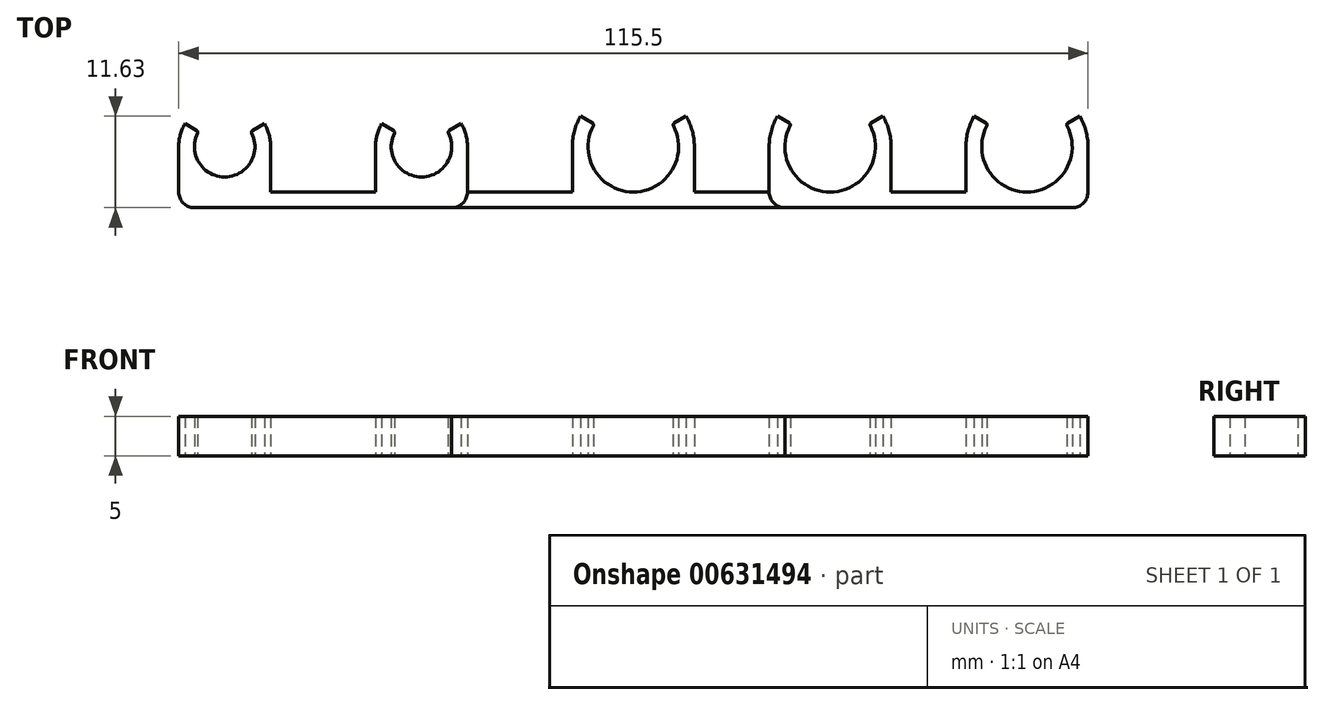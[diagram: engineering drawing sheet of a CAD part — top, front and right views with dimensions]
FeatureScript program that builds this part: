
annotation { "Feature Type Name" : "Feature", "Feature Type Description" : "" }
export const myFeature = defineFeature(function(context is Context, id is Id, definition is map)
    precondition{}
    {
        {
            var Q0;
            Q0=qCreatedBy(makeId("Top.planeOp"),FACE);
            var sketch = newSketch(context, id + "F0", { "sketchPlane" : qUnion([Q0])});
            skArc(sketch, "E0", {"start": v(-5.1, 2.67) * mm, "mid": v(0, -5.75) * mm, "end": v(5.1, 2.67) * mm});
            skArc(sketch, "E1.0", {"start": v(-6.7, 3.88) * mm, "mid": v(0, -7.75) * mm, "end": v(6.7, 3.88) * mm});
            skLineSegment(sketch, "E2", {"start": v(-5.19, 3) * mm, "end": v(-6.7, 3.88) * mm});
            skLineSegment(sketch, "E3", {"start": v(5.19, 3) * mm, "end": v(6.7, 3.88) * mm});
            skLineSegment(sketch, "E4", {"start": v(0, -7.75) * mm, "end": v(-7.75, -7.75) * mm});
            skLineSegment(sketch, "E5", {"start": v(-5.75, -7.75) * mm, "end": v(5.75, -7.75) * mm});
            skLineSegment(sketch, "E6", {"start": v(7.75, 0) * mm, "end": v(7.75, -5.75) * mm});
            skLineSegment(sketch, "E7", {"start": v(-7.75, 0) * mm, "end": v(-7.75, -5.75) * mm});
            skPoint(sketch, "E8.visualSharp", {"position": v(-4.97, 2.88) * mm});
            skArc(sketch, "E8.filletArc", {"start": v(-5.1, 2.67) * mm, "mid": v(-5.07, 2.86) * mm, "end": v(-5.19, 3) * mm});
            skPoint(sketch, "E9.visualSharp", {"position": v(4.97, 2.88) * mm});
            skArc(sketch, "E9.filletArc", {"start": v(5.19, 3) * mm, "mid": v(5.07, 2.86) * mm, "end": v(5.1, 2.67) * mm});
            skPoint(sketch, "E10.visualSharp", {"position": v(-7.75, -7.75) * mm});
            skPoint(sketch, "E11.1.0.0", {"position": v(20.03, 2.88) * mm});
            skArc(sketch, "E11.1.0.1", {"start": v(19.9, 2.67) * mm, "mid": v(25, -5.75) * mm, "end": v(30.1, 2.67) * mm});
            skArc(sketch, "E11.1.0.2", {"start": v(18.3, 3.88) * mm, "mid": v(25, -7.75) * mm, "end": v(31.7, 3.88) * mm});
            skPoint(sketch, "E11.1.0.3", {"position": v(32.75, -7.75) * mm});
            skPoint(sketch, "E11.1.0.4", {"position": v(17.25, -7.75) * mm});
            skPoint(sketch, "E11.1.0.5", {"position": v(29.97, 2.88) * mm});
            skLineSegment(sketch, "E11.1.0.6", {"start": v(32.75, 0) * mm, "end": v(32.75, -5.75) * mm});
            skLineSegment(sketch, "E11.1.0.7", {"start": v(17.25, 0) * mm, "end": v(17.25, -5.75) * mm});
            skArc(sketch, "E11.1.0.8", {"start": v(17.25, -5.75) * mm, "mid": v(17.84, -7.16) * mm, "end": v(19.25, -7.75) * mm});
            skArc(sketch, "E11.1.0.9", {"start": v(30.75, -7.75) * mm, "mid": v(32.16, -7.16) * mm, "end": v(32.75, -5.75) * mm});
            skLineSegment(sketch, "E11.1.0.10", {"start": v(19.81, 3) * mm, "end": v(18.3, 3.88) * mm});
            skLineSegment(sketch, "E11.1.0.11", {"start": v(30.19, 3) * mm, "end": v(31.7, 3.88) * mm});
            skArc(sketch, "E11.1.0.12", {"start": v(19.9, 2.67) * mm, "mid": v(19.93, 2.86) * mm, "end": v(19.81, 3) * mm});
            skArc(sketch, "E11.1.0.13", {"start": v(30.19, 3) * mm, "mid": v(30.07, 2.86) * mm, "end": v(30.1, 2.67) * mm});
            skLineSegment(sketch, "E11.1.0.14", {"start": v(19.25, -7.75) * mm, "end": v(30.75, -7.75) * mm});
            skPoint(sketch, "E11.2.0.0", {"position": v(45.03, 2.88) * mm});
            skArc(sketch, "E11.2.0.1", {"start": v(44.9, 2.67) * mm, "mid": v(50, -5.75) * mm, "end": v(55.1, 2.67) * mm});
            skArc(sketch, "E11.2.0.2", {"start": v(43.3, 3.88) * mm, "mid": v(50, -7.75) * mm, "end": v(56.7, 3.88) * mm});
            skPoint(sketch, "E11.2.0.3", {"position": v(57.75, -7.75) * mm});
            skPoint(sketch, "E11.2.0.4", {"position": v(42.25, -7.75) * mm});
            skPoint(sketch, "E11.2.0.5", {"position": v(54.97, 2.88) * mm});
            skLineSegment(sketch, "E11.2.0.6", {"start": v(57.75, 0) * mm, "end": v(57.75, -5.75) * mm});
            skLineSegment(sketch, "E11.2.0.7", {"start": v(42.25, 0) * mm, "end": v(42.25, -5.75) * mm});
            skArc(sketch, "E11.2.0.8", {"start": v(42.25, -5.75) * mm, "mid": v(42.84, -7.16) * mm, "end": v(44.25, -7.75) * mm});
            skArc(sketch, "E11.2.0.9", {"start": v(55.75, -7.75) * mm, "mid": v(57.16, -7.16) * mm, "end": v(57.75, -5.75) * mm});
            skLineSegment(sketch, "E11.2.0.10", {"start": v(44.81, 3) * mm, "end": v(43.3, 3.88) * mm});
            skLineSegment(sketch, "E11.2.0.11", {"start": v(55.19, 3) * mm, "end": v(56.7, 3.88) * mm});
            skArc(sketch, "E11.2.0.12", {"start": v(44.9, 2.67) * mm, "mid": v(44.93, 2.86) * mm, "end": v(44.81, 3) * mm});
            skArc(sketch, "E11.2.0.13", {"start": v(55.19, 3) * mm, "mid": v(55.07, 2.86) * mm, "end": v(55.1, 2.67) * mm});
            skLineSegment(sketch, "E11.2.0.14", {"start": v(44.25, -7.75) * mm, "end": v(55.75, -7.75) * mm});
            skArc(sketch, "E12", {"start": v(-30.35, 1.7) * mm, "mid": v(-26.9, -3.84) * mm, "end": v(-23.48, 1.72) * mm});
            skArc(sketch, "E13.0", {"start": v(-31.97, 2.92) * mm, "mid": v(-26.9, -5.84) * mm, "end": v(-21.86, 2.93) * mm});
            skLineSegment(sketch, "E14", {"start": v(-32.75, 0) * mm, "end": v(-32.75, -5.75) * mm});
            skLineSegment(sketch, "E15", {"start": v(-21.07, 0) * mm, "end": v(-21.07, -5.75) * mm});
            skLineSegment(sketch, "E16", {"start": v(-30.75, -7.75) * mm, "end": v(-23.07, -7.75) * mm});
            skLineSegment(sketch, "E17", {"start": v(-30.45, 2.04) * mm, "end": v(-31.97, 2.92) * mm});
            skLineSegment(sketch, "E18", {"start": v(-23.39, 2.05) * mm, "end": v(-21.86, 2.93) * mm});
            skPoint(sketch, "E19.visualSharp", {"position": v(-23.6, 1.93) * mm});
            skArc(sketch, "E19.filletArc", {"start": v(-23.39, 2.05) * mm, "mid": v(-23.5, 1.9) * mm, "end": v(-23.48, 1.72) * mm});
            skPoint(sketch, "E20.visualSharp", {"position": v(-30.24, 1.92) * mm});
            skArc(sketch, "E20.filletArc", {"start": v(-30.35, 1.7) * mm, "mid": v(-30.33, 1.9) * mm, "end": v(-30.45, 2.04) * mm});
            skPoint(sketch, "E21.visualSharp", {"position": v(-21.07, -7.75) * mm});
            skArc(sketch, "E21.filletArc", {"start": v(-23.07, -7.75) * mm, "mid": v(-21.66, -7.16) * mm, "end": v(-21.07, -5.75) * mm});
            skPoint(sketch, "E22.visualSharp", {"position": v(-32.75, -7.75) * mm});
            skArc(sketch, "E22.filletArc", {"start": v(-32.75, -5.75) * mm, "mid": v(-32.16, -7.16) * mm, "end": v(-30.75, -7.75) * mm});
            skLineSegment(sketch, "E23.1.0.0", {"start": v(-46.07, 0) * mm, "end": v(-46.07, -5.75) * mm});
            skLineSegment(sketch, "E23.1.0.1", {"start": v(-32.75, -7.75) * mm, "end": v(-83.88, -7.75) * mm, "construction": true});
            skPoint(sketch, "E23.1.0.2", {"position": v(-48.6, 1.93) * mm});
            skArc(sketch, "E23.1.0.3", {"start": v(-55.35, 1.7) * mm, "mid": v(-51.9, -3.84) * mm, "end": v(-48.48, 1.72) * mm});
            skArc(sketch, "E23.1.0.4", {"start": v(-48.07, -7.75) * mm, "mid": v(-46.66, -7.16) * mm, "end": v(-46.07, -5.75) * mm});
            skPoint(sketch, "E23.1.0.5", {"position": v(-57.75, -7.75) * mm});
            skLineSegment(sketch, "E23.1.0.6", {"start": v(-57.75, 0) * mm, "end": v(-57.75, -5.75) * mm});
            skArc(sketch, "E23.1.0.7", {"start": v(-56.97, 2.92) * mm, "mid": v(-51.9, -5.84) * mm, "end": v(-46.86, 2.93) * mm});
            skPoint(sketch, "E23.1.0.8", {"position": v(-46.07, -7.75) * mm});
            skPoint(sketch, "E23.1.0.9", {"position": v(-55.24, 1.92) * mm});
            skArc(sketch, "E23.1.0.10", {"start": v(-57.75, -5.75) * mm, "mid": v(-57.16, -7.16) * mm, "end": v(-55.75, -7.75) * mm});
            skLineSegment(sketch, "E23.1.0.11", {"start": v(-55.75, -7.75) * mm, "end": v(-48.07, -7.75) * mm});
            skLineSegment(sketch, "E23.1.0.12", {"start": v(-55.45, 2.04) * mm, "end": v(-56.97, 2.92) * mm});
            skArc(sketch, "E23.1.0.13", {"start": v(-48.39, 2.05) * mm, "mid": v(-48.5, 1.9) * mm, "end": v(-48.48, 1.72) * mm});
            skLineSegment(sketch, "E23.1.0.14", {"start": v(-48.39, 2.05) * mm, "end": v(-46.86, 2.93) * mm});
            skArc(sketch, "E23.1.0.15", {"start": v(-55.35, 1.7) * mm, "mid": v(-55.33, 1.9) * mm, "end": v(-55.45, 2.04) * mm});
            skLineSegment(sketch, "E23.2.0.1", {"start": v(-57.75, -7.75) * mm, "end": v(-108.88, -7.75) * mm, "construction": true});
            skLineSegment(sketch, "E23.direction1", {"start": v(-58.88, -7.75) * mm, "end": v(-83.88, -7.75) * mm, "construction": true});
            skLineSegment(sketch, "E24", {"start": v(-57.75, -7.75) * mm, "end": v(-57.75, -5.75) * mm});
            skLineSegment(sketch, "E25", {"start": v(-46.07, -5.75) * mm, "end": v(-32.75, -5.75) * mm});
            skLineSegment(sketch, "E26", {"start": v(-21.07, -5.75) * mm, "end": v(-7.75, -5.75) * mm});
            skLineSegment(sketch, "E27", {"start": v(7.75, -5.75) * mm, "end": v(17.25, -5.75) * mm});
            skLineSegment(sketch, "E28", {"start": v(32.75, -5.75) * mm, "end": v(42.25, -5.75) * mm});
            skLineSegment(sketch, "E29", {"start": v(-48.07, -7.75) * mm, "end": v(-30.75, -7.75) * mm});
            skLineSegment(sketch, "E30", {"start": v(-30.75, -7.75) * mm, "end": v(55.88, -7.75) * mm});
            skSolve(sketch);
        }
        {
            var Q0;
            Q0=makeQuery(id+"F0.imprint","IMPRINT",FACE,{"disambiguationData":[TD([[makeQuery(id+"F0.imprint","IMPRINT",EDGE,{"derivedFrom":sQuery(id+"F0.wireOp",EDGE,"E0")}),-1.0]])]});
            var Q1;
            {var subQ0=sQuery(id+"F0.wireOp",EDGE,"E7");Q1=makeQuery(id+"F0.imprint","IMPRINT",FACE,{"disambiguationData":[TD([[makeQuery(id+"F0.imprint","IMPRINT",EDGE,{"derivedFrom":subQ0}),1.0]])]});}
            var Q2;
            {var subQ0=sQuery(id+"F0.wireOp",EDGE,"E6");Q2=makeQuery(id+"F0.imprint","IMPRINT",FACE,{"disambiguationData":[TD([[makeQuery(id+"F0.imprint","IMPRINT",EDGE,{"derivedFrom":subQ0}),-1.0]])]});}
            extrude(context, id + "F1", {"entities" : qUnion([Q0, Q1, Q2]), "depth" : 5 * mm, "offsetDistance" : 25 * mm});
        }
        {
            var Q0;
            Q0=makeQuery(id+"F0.imprint","IMPRINT",FACE,{"disambiguationData":[TD([[makeQuery(id+"F0.imprint","IMPRINT",EDGE,{"derivedFrom":sQuery(id+"F0.wireOp",EDGE,"E23.1.0.3")}),-1.0]])]});
            var Q1;
            {var subQ2=sQuery(id+"F0.wireOp",EDGE,"E23.1.0.0");Q1=makeQuery(id+"F0.imprint","IMPRINT",FACE,{"disambiguationData":[TD([[makeQuery(id+"F0.imprint","IMPRINT",EDGE,{"derivedFrom":subQ2}),-1.0]])]});}
            var Q2;
            Q2=makeQuery(id+"F0.imprint","IMPRINT",FACE,{"disambiguationData":[TD([[makeQuery(id+"F0.imprint","IMPRINT",EDGE,{"derivedFrom":sQuery(id+"F0.wireOp",EDGE,"E12")}),-1.0]])]});
            var Q3;
            {var subQ1=sQuery(id+"F0.wireOp",EDGE,"E14");Q3=makeQuery(id+"F0.imprint","IMPRINT",FACE,{"disambiguationData":[TD([[makeQuery(id+"F0.imprint","IMPRINT",EDGE,{"derivedFrom":subQ1}),1.0]])]});}
            var Q4;
            Q4=makeQuery(id+"F0.imprint","IMPRINT",FACE,{"disambiguationData":[TD([[makeQuery(id+"F0.imprint","IMPRINT",EDGE,{"derivedFrom":sQuery(id+"F0.wireOp",EDGE,"E11.1.0.1")}),-1.0]])]});
            var Q5;
            {var subQ0=sQuery(id+"F0.wireOp",EDGE,"E11.1.0.7");Q5=makeQuery(id+"F0.imprint","IMPRINT",FACE,{"disambiguationData":[TD([[makeQuery(id+"F0.imprint","IMPRINT",EDGE,{"derivedFrom":subQ0}),1.0]])]});}
            var Q6;
            {var subQ0=sQuery(id+"F0.wireOp",EDGE,"E11.1.0.6");Q6=makeQuery(id+"F0.imprint","IMPRINT",FACE,{"disambiguationData":[TD([[makeQuery(id+"F0.imprint","IMPRINT",EDGE,{"derivedFrom":subQ0}),-1.0]])]});}
            var Q7;
            Q7=makeQuery(id+"F0.imprint","IMPRINT",FACE,{"disambiguationData":[TD([[makeQuery(id+"F0.imprint","IMPRINT",EDGE,{"derivedFrom":sQuery(id+"F0.wireOp",EDGE,"E11.2.0.1")}),-1.0]])]});
            var Q8;
            {var subQ0=sQuery(id+"F0.wireOp",EDGE,"E11.2.0.7");Q8=makeQuery(id+"F0.imprint","IMPRINT",FACE,{"disambiguationData":[TD([[makeQuery(id+"F0.imprint","IMPRINT",EDGE,{"derivedFrom":subQ0}),1.0]])]});}
            var Q9;
            {var subQ0=sQuery(id+"F0.wireOp",EDGE,"E11.2.0.6");Q9=makeQuery(id+"F0.imprint","IMPRINT",FACE,{"disambiguationData":[TD([[makeQuery(id+"F0.imprint","IMPRINT",EDGE,{"derivedFrom":subQ0}),-1.0]])]});}
            var Q10;
            Q10=makeQuery(id+"F0.imprint","IMPRINT",FACE,{"disambiguationData":[TD([[makeQuery(id+"F0.imprint","IMPRINT",EDGE,{"derivedFrom":sQuery(id+"F0.wireOp",EDGE,"E22.filletArc")}),-1.0]])]});
            var Q11;
            {var subQ0=sQuery(id+"F0.wireOp",EDGE,"E10.filletArc");Q11=makeQuery(id+"F0.imprint","IMPRINT",FACE,{"disambiguationData":[TD([[makeQuery(id+"F0.imprint","IMPRINT",EDGE,{"derivedFrom":subQ0}),-1.0]])]});}
            var Q12;
            {var subQ0=sQuery(id+"F0.wireOp",EDGE,"656fffb1-0bce-4614-b2c4-3bbddfca00fc.filletArc");Q12=makeQuery(id+"F0.imprint","IMPRINT",FACE,{"disambiguationData":[TD([[makeQuery(id+"F0.imprint","IMPRINT",EDGE,{"derivedFrom":subQ0}),-1.0]])]});}
            var Q13;
            {var subQ0=sQuery(id+"F0.wireOp",EDGE,"E11.1.0.9");Q13=makeQuery(id+"F0.imprint","IMPRINT",FACE,{"disambiguationData":[TD([[makeQuery(id+"F0.imprint","IMPRINT",EDGE,{"derivedFrom":subQ0}),-1.0]])]});}
            extrude(context, id + "F2", {"entities" : qUnion([Q0, Q1, Q2, Q3, Q4, Q5, Q6, Q7, Q8, Q9, Q10, Q11, Q12, Q13]), "depth" : 5 * mm, "offsetDistance" : 25 * mm});
        }
    });
